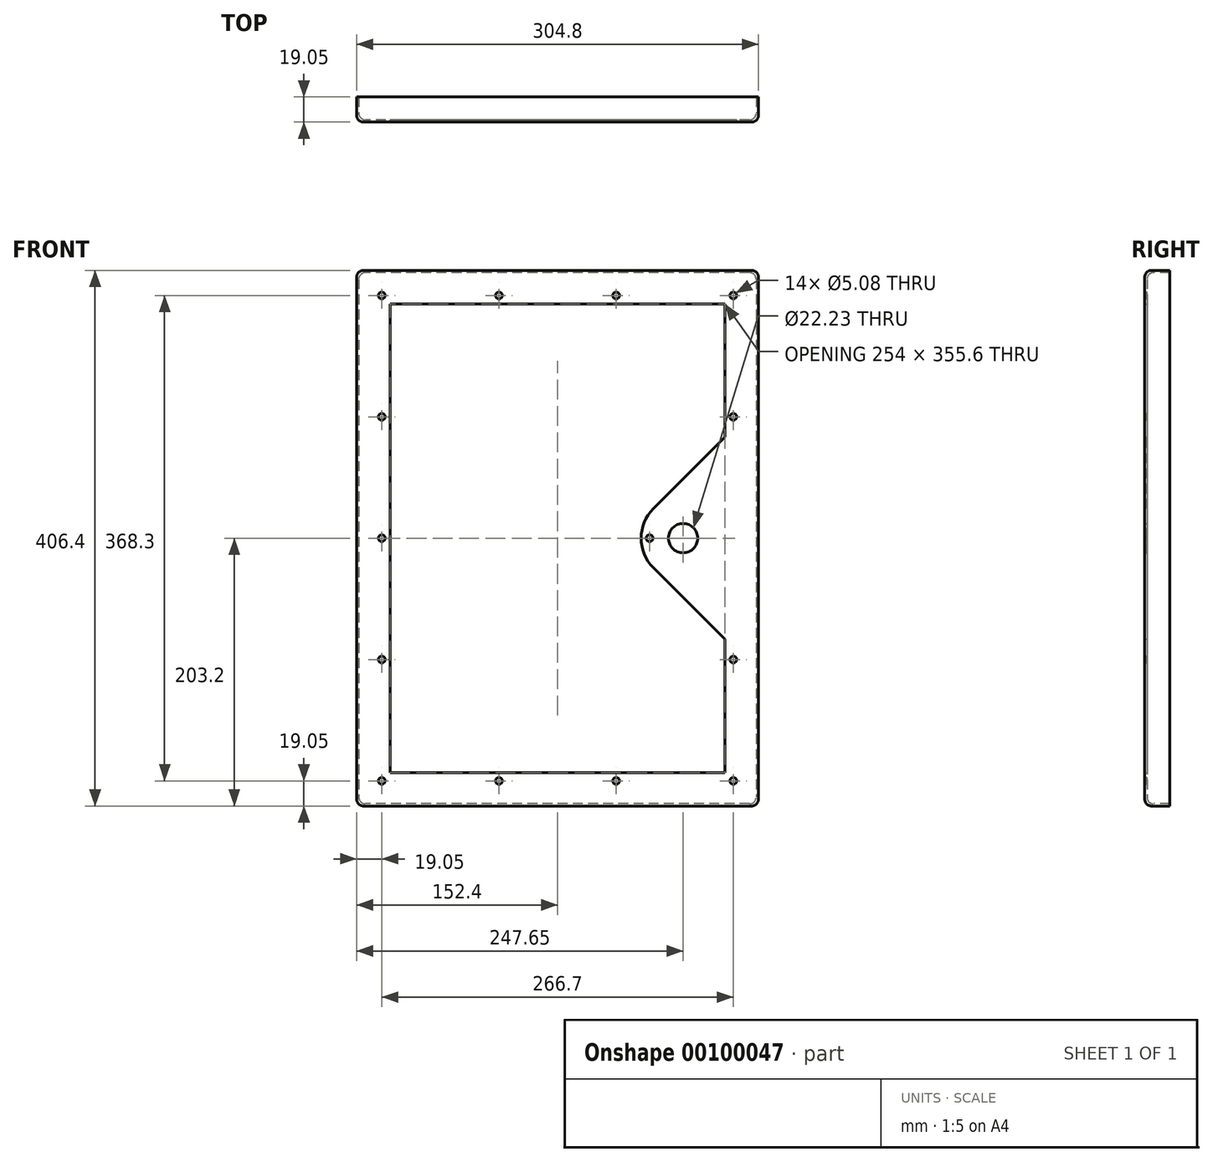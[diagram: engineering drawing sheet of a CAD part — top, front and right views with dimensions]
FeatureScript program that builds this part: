
annotation { "Feature Type Name" : "Feature", "Feature Type Description" : "" }
export const myFeature = defineFeature(function(context is Context, id is Id, definition is map)
    precondition{}
    {
        {
            var Q0;
            Q0=qCreatedBy(makeId("Front.planeOp"),FACE);
            var sketch = newSketch(context, id + "F0", { "sketchPlane" : qUnion([Q0])});
            skLineSegment(sketch, "E0.bottom", {"start": v(152.4, 203.2) * mm, "end": v(-152.4, 203.2) * mm});
            skLineSegment(sketch, "E0.top", {"start": v(152.4, -203.2) * mm, "end": v(-152.4, -203.2) * mm});
            skLineSegment(sketch, "E0.left", {"start": v(152.4, 203.2) * mm, "end": v(152.4, -203.2) * mm});
            skLineSegment(sketch, "E0.right", {"start": v(-152.4, 203.2) * mm, "end": v(-152.4, -203.2) * mm});
            skPoint(sketch, "E0.middle", {"position": v(0, 0) * mm});
            skLineSegment(sketch, "E1.bottom", {"start": v(127, 177.8) * mm, "end": v(-127, 177.8) * mm});
            skLineSegment(sketch, "E1.top", {"start": v(127, -177.8) * mm, "end": v(-127, -177.8) * mm});
            skLineSegment(sketch, "E1.left", {"start": v(127, 177.8) * mm, "end": v(127, 76.65) * mm});
            skLineSegment(sketch, "E1.right", {"start": v(-127, 177.8) * mm, "end": v(-127, -177.8) * mm});
            skArc(sketch, "E2", {"start": v(72.8, 22.45) * mm, "mid": v(63.5, 0) * mm, "end": v(72.8, -22.45) * mm});
            skLineSegment(sketch, "E3", {"start": v(72.8, 22.45) * mm, "end": v(127, 76.65) * mm});
            skLineSegment(sketch, "E4", {"start": v(72.8, -22.45) * mm, "end": v(127, -76.65) * mm});
            skLineSegment(sketch, "E5.trimOffspring", {"start": v(127, -76.65) * mm, "end": v(127, -177.8) * mm});
            skCircle(sketch, "E6", {"center": v(95.25, 0) * mm, "radius": 11.11 * mm});
            skSolve(sketch);
        }
        {
            var Q0;
            Q0=makeQuery(id+"F0.imprint","IMPRINT",FACE,{"disambiguationData":[TD([[makeQuery(id+"F0.imprint","IMPRINT",EDGE,{"derivedFrom":sQuery(id+"F0.wireOp",EDGE,"E0.bottom")}),1.0]])]});
            extrude(context, id + "F1", {"entities" : qUnion([Q0]), "depth" : 1.65 * mm});
        }
        {
            var Q0;
            Q0=makeQuery(id+"F1.opExtrude","CAP_FACE",FACE,{"disambiguationData":[OSD([sQuery(id+"F0.wireOp",EDGE,"E0.bottom"),sQuery(id+"F0.wireOp",EDGE,"E0.top"),sQuery(id+"F0.wireOp",EDGE,"E0.left"),sQuery(id+"F0.wireOp",EDGE,"E0.right"),sQuery(id+"F0.wireOp",EDGE,"E1.bottom"),sQuery(id+"F0.wireOp",EDGE,"E1.top"),sQuery(id+"F0.wireOp",EDGE,"E1.left"),sQuery(id+"F0.wireOp",EDGE,"E1.right"),sQuery(id+"F0.wireOp",EDGE,"E2"),sQuery(id+"F0.wireOp",EDGE,"E3"),sQuery(id+"F0.wireOp",EDGE,"E4"),sQuery(id+"F0.wireOp",EDGE,"E5.trimOffspring"),sQuery(id+"F0.wireOp",EDGE,"E6")])],"isStart":false});
            var sketch = newSketch(context, id + "F2", { "sketchPlane" : qUnion([Q0])});
            skLineSegment(sketch, "E7.0", {"start": v(152.4, -203.2) * mm, "end": v(-152.4, -203.2) * mm});
            skLineSegment(sketch, "E7.1", {"start": v(152.4, 203.2) * mm, "end": v(152.4, -203.2) * mm});
            skLineSegment(sketch, "E7.2", {"start": v(152.4, 203.2) * mm, "end": v(-152.4, 203.2) * mm});
            skLineSegment(sketch, "E7.3", {"start": v(-152.4, 203.2) * mm, "end": v(-152.4, -203.2) * mm});
            skLineSegment(sketch, "E8.0", {"start": v(150.75, -201.55) * mm, "end": v(-150.75, -201.55) * mm});
            skLineSegment(sketch, "E8.1", {"start": v(150.75, 201.55) * mm, "end": v(150.75, -201.55) * mm});
            skLineSegment(sketch, "E8.2", {"start": v(150.75, 201.55) * mm, "end": v(-150.75, 201.55) * mm});
            skLineSegment(sketch, "E8.3", {"start": v(-150.75, 201.55) * mm, "end": v(-150.75, -201.55) * mm});
            skSolve(sketch);
        }
        {
            var Q0;
            Q0 = qSketchRegion(id + "F2", true);
            extrude(context, id + "F3", {"entities" : qUnion([Q0]), "operationType" : NewBodyOperationType.ADD, "oppositeDirection" : true, "depth" : 19.05 * mm});
        }
        {
            var Q0;
            Q0=makeQuery(id+"F3.boolean.opBoolean","INTERSECT",EDGE,{"derivedFrom":[makeQuery(id+"F1.opExtrude","CAP_FACE",FACE,{"disambiguationData":[OSD([sQuery(id+"F0.wireOp",EDGE,"E0.bottom"),sQuery(id+"F0.wireOp",EDGE,"E0.top"),sQuery(id+"F0.wireOp",EDGE,"E0.left"),sQuery(id+"F0.wireOp",EDGE,"E0.right"),sQuery(id+"F0.wireOp",EDGE,"E1.bottom"),sQuery(id+"F0.wireOp",EDGE,"E1.top"),sQuery(id+"F0.wireOp",EDGE,"E1.left"),sQuery(id+"F0.wireOp",EDGE,"E1.right"),sQuery(id+"F0.wireOp",EDGE,"E2"),sQuery(id+"F0.wireOp",EDGE,"E3"),sQuery(id+"F0.wireOp",EDGE,"E4"),sQuery(id+"F0.wireOp",EDGE,"E5.trimOffspring"),sQuery(id+"F0.wireOp",EDGE,"E6")])],"isStart":true}),makeQuery(id+"F3.opExtrude","SWEPT_FACE",FACE,{"disambiguationData":[OSD([sQuery(id+"F2.wireOp",EDGE,"E8.3")])]})]});
            var Q1;
            Q1=makeQuery(id+"F3.boolean.opBoolean","INTERSECT",EDGE,{"derivedFrom":[makeQuery(id+"F1.opExtrude","CAP_FACE",FACE,{"disambiguationData":[OSD([sQuery(id+"F0.wireOp",EDGE,"E0.bottom"),sQuery(id+"F0.wireOp",EDGE,"E0.top"),sQuery(id+"F0.wireOp",EDGE,"E0.left"),sQuery(id+"F0.wireOp",EDGE,"E0.right"),sQuery(id+"F0.wireOp",EDGE,"E1.bottom"),sQuery(id+"F0.wireOp",EDGE,"E1.top"),sQuery(id+"F0.wireOp",EDGE,"E1.left"),sQuery(id+"F0.wireOp",EDGE,"E1.right"),sQuery(id+"F0.wireOp",EDGE,"E2"),sQuery(id+"F0.wireOp",EDGE,"E3"),sQuery(id+"F0.wireOp",EDGE,"E4"),sQuery(id+"F0.wireOp",EDGE,"E5.trimOffspring"),sQuery(id+"F0.wireOp",EDGE,"E6")])],"isStart":true}),makeQuery(id+"F3.opExtrude","SWEPT_FACE",FACE,{"disambiguationData":[OSD([sQuery(id+"F2.wireOp",EDGE,"E8.2")])]})]});
            var Q2;
            Q2=makeQuery(id+"F3.boolean.opBoolean","INTERSECT",EDGE,{"derivedFrom":[makeQuery(id+"F1.opExtrude","CAP_FACE",FACE,{"disambiguationData":[OSD([sQuery(id+"F0.wireOp",EDGE,"E0.bottom"),sQuery(id+"F0.wireOp",EDGE,"E0.top"),sQuery(id+"F0.wireOp",EDGE,"E0.left"),sQuery(id+"F0.wireOp",EDGE,"E0.right"),sQuery(id+"F0.wireOp",EDGE,"E1.bottom"),sQuery(id+"F0.wireOp",EDGE,"E1.top"),sQuery(id+"F0.wireOp",EDGE,"E1.left"),sQuery(id+"F0.wireOp",EDGE,"E1.right"),sQuery(id+"F0.wireOp",EDGE,"E2"),sQuery(id+"F0.wireOp",EDGE,"E3"),sQuery(id+"F0.wireOp",EDGE,"E4"),sQuery(id+"F0.wireOp",EDGE,"E5.trimOffspring"),sQuery(id+"F0.wireOp",EDGE,"E6")])],"isStart":true}),makeQuery(id+"F3.opExtrude","SWEPT_FACE",FACE,{"disambiguationData":[OSD([sQuery(id+"F2.wireOp",EDGE,"E8.1")])]})]});
            var Q3;
            Q3=makeQuery(id+"F3.boolean.opBoolean","INTERSECT",EDGE,{"derivedFrom":[makeQuery(id+"F1.opExtrude","CAP_FACE",FACE,{"disambiguationData":[OSD([sQuery(id+"F0.wireOp",EDGE,"E0.bottom"),sQuery(id+"F0.wireOp",EDGE,"E0.top"),sQuery(id+"F0.wireOp",EDGE,"E0.left"),sQuery(id+"F0.wireOp",EDGE,"E0.right"),sQuery(id+"F0.wireOp",EDGE,"E1.bottom"),sQuery(id+"F0.wireOp",EDGE,"E1.top"),sQuery(id+"F0.wireOp",EDGE,"E1.left"),sQuery(id+"F0.wireOp",EDGE,"E1.right"),sQuery(id+"F0.wireOp",EDGE,"E2"),sQuery(id+"F0.wireOp",EDGE,"E3"),sQuery(id+"F0.wireOp",EDGE,"E4"),sQuery(id+"F0.wireOp",EDGE,"E5.trimOffspring"),sQuery(id+"F0.wireOp",EDGE,"E6")])],"isStart":true}),makeQuery(id+"F3.opExtrude","SWEPT_FACE",FACE,{"disambiguationData":[OSD([sQuery(id+"F2.wireOp",EDGE,"E8.0")])]})]});
            var Q4;
            Q4=makeQuery(id+"F3.opExtrude","SWEPT_EDGE",EDGE,{"disambiguationData":[OSD([sQuery(id+"F2.wireOp",EDGE,"E8.0"),sQuery(id+"F2.wireOp",EDGE,"E8.3")])]});
            var Q5;
            Q5=makeQuery(id+"F3.opExtrude","SWEPT_EDGE",EDGE,{"disambiguationData":[OSD([sQuery(id+"F2.wireOp",EDGE,"E8.2"),sQuery(id+"F2.wireOp",EDGE,"E8.3")])]});
            var Q6;
            Q6=makeQuery(id+"F3.opExtrude","SWEPT_EDGE",EDGE,{"disambiguationData":[OSD([sQuery(id+"F2.wireOp",EDGE,"E8.1"),sQuery(id+"F2.wireOp",EDGE,"E8.2")])]});
            var Q7;
            Q7=makeQuery(id+"F3.opExtrude","SWEPT_EDGE",EDGE,{"disambiguationData":[OSD([sQuery(id+"F2.wireOp",EDGE,"E8.0"),sQuery(id+"F2.wireOp",EDGE,"E8.1")])]});
            fillet(context, id + "F4", {"entities" : qUnion([Q0, Q1, Q2, Q3, Q4, Q5, Q6, Q7]), "radius" : 5.08 * mm, "tangentPropagation" : true, "allowEdgeOverflow" : false});
        }
        {
            var Q0;
            Q0=makeQuery(id+"F3.boolean.opBoolean","MERGE",EDGE,{"derivedFrom":[makeQuery(id+"F1.opExtrude","SWEPT_EDGE",EDGE,{"disambiguationData":[OSD([sQuery(id+"F0.wireOp",EDGE,"E0.bottom"),sQuery(id+"F0.wireOp",EDGE,"E0.right")])]}),makeQuery(id+"F3.opExtrude","SWEPT_EDGE",EDGE,{"disambiguationData":[OSD([sQuery(id+"F2.wireOp",EDGE,"E7.2"),sQuery(id+"F2.wireOp",EDGE,"E7.3")])]})]});
            var Q1;
            Q1=makeQuery(id+"F1.opExtrude","CAP_EDGE",EDGE,{"disambiguationData":[OSD([sQuery(id+"F0.wireOp",EDGE,"E0.bottom")])],"isStart":false});
            var Q2;
            Q2=makeQuery(id+"F1.opExtrude","CAP_EDGE",EDGE,{"disambiguationData":[OSD([sQuery(id+"F0.wireOp",EDGE,"E0.right")])],"isStart":false});
            var Q3;
            Q3=makeQuery(id+"F3.boolean.opBoolean","MERGE",EDGE,{"derivedFrom":[makeQuery(id+"F1.opExtrude","SWEPT_EDGE",EDGE,{"disambiguationData":[OSD([sQuery(id+"F0.wireOp",EDGE,"E0.bottom"),sQuery(id+"F0.wireOp",EDGE,"E0.left")])]}),makeQuery(id+"F3.opExtrude","SWEPT_EDGE",EDGE,{"disambiguationData":[OSD([sQuery(id+"F2.wireOp",EDGE,"E7.1"),sQuery(id+"F2.wireOp",EDGE,"E7.2")])]})]});
            var Q4;
            Q4=makeQuery(id+"F1.opExtrude","CAP_EDGE",EDGE,{"disambiguationData":[OSD([sQuery(id+"F0.wireOp",EDGE,"E0.left")])],"isStart":false});
            var Q5;
            Q5=makeQuery(id+"F3.boolean.opBoolean","MERGE",EDGE,{"derivedFrom":[makeQuery(id+"F1.opExtrude","SWEPT_EDGE",EDGE,{"disambiguationData":[OSD([sQuery(id+"F0.wireOp",EDGE,"E0.top"),sQuery(id+"F0.wireOp",EDGE,"E0.left")])]}),makeQuery(id+"F3.opExtrude","SWEPT_EDGE",EDGE,{"disambiguationData":[OSD([sQuery(id+"F2.wireOp",EDGE,"E7.0"),sQuery(id+"F2.wireOp",EDGE,"E7.1")])]})]});
            var Q6;
            Q6=makeQuery(id+"F1.opExtrude","CAP_EDGE",EDGE,{"disambiguationData":[OSD([sQuery(id+"F0.wireOp",EDGE,"E0.top")])],"isStart":false});
            var Q7;
            Q7=makeQuery(id+"F3.boolean.opBoolean","MERGE",EDGE,{"derivedFrom":[makeQuery(id+"F1.opExtrude","SWEPT_EDGE",EDGE,{"disambiguationData":[OSD([sQuery(id+"F0.wireOp",EDGE,"E0.top"),sQuery(id+"F0.wireOp",EDGE,"E0.right")])]}),makeQuery(id+"F3.opExtrude","SWEPT_EDGE",EDGE,{"disambiguationData":[OSD([sQuery(id+"F2.wireOp",EDGE,"E7.0"),sQuery(id+"F2.wireOp",EDGE,"E7.3")])]})]});
            fillet(context, id + "F5", {"entities" : qUnion([Q0, Q1, Q2, Q3, Q4, Q5, Q6, Q7]), "radius" : 5.08 * mm, "tangentPropagation" : true, "allowEdgeOverflow" : false});
        }
        {
            var Q0;
            Q0=makeQuery(id+"F1.opExtrude","CAP_FACE",FACE,{"disambiguationData":[OSD([sQuery(id+"F0.wireOp",EDGE,"E0.bottom"),sQuery(id+"F0.wireOp",EDGE,"E0.top"),sQuery(id+"F0.wireOp",EDGE,"E0.left"),sQuery(id+"F0.wireOp",EDGE,"E0.right"),sQuery(id+"F0.wireOp",EDGE,"E1.bottom"),sQuery(id+"F0.wireOp",EDGE,"E1.top"),sQuery(id+"F0.wireOp",EDGE,"E1.left"),sQuery(id+"F0.wireOp",EDGE,"E1.right"),sQuery(id+"F0.wireOp",EDGE,"E2"),sQuery(id+"F0.wireOp",EDGE,"E3"),sQuery(id+"F0.wireOp",EDGE,"E4"),sQuery(id+"F0.wireOp",EDGE,"E5.trimOffspring"),sQuery(id+"F0.wireOp",EDGE,"E6")])],"isStart":false});
            var sketch = newSketch(context, id + "F6", { "sketchPlane" : qUnion([Q0])});
            skCircle(sketch, "E9", {"center": v(-133.35, 184.15) * mm, "radius": 2.54 * mm});
            skCircle(sketch, "E10", {"center": v(-133.35, 92.08) * mm, "radius": 2.54 * mm});
            skCircle(sketch, "E11", {"center": v(-133.35, 0) * mm, "radius": 2.54 * mm});
            skCircle(sketch, "E12", {"center": v(-133.35, -92.08) * mm, "radius": 2.54 * mm});
            skCircle(sketch, "E13", {"center": v(-133.35, -184.15) * mm, "radius": 2.54 * mm});
            skCircle(sketch, "E14", {"center": v(-44.45, 184.15) * mm, "radius": 2.54 * mm});
            skCircle(sketch, "E15", {"center": v(44.45, 184.15) * mm, "radius": 2.54 * mm});
            skCircle(sketch, "E16", {"center": v(133.35, 184.15) * mm, "radius": 2.54 * mm});
            skCircle(sketch, "E17", {"center": v(133.35, 92.08) * mm, "radius": 2.54 * mm});
            skCircle(sketch, "E18", {"center": v(133.35, -92.07) * mm, "radius": 2.54 * mm});
            skCircle(sketch, "E19", {"center": v(133.35, -184.15) * mm, "radius": 2.54 * mm});
            skCircle(sketch, "E20", {"center": v(44.45, -184.15) * mm, "radius": 2.54 * mm});
            skCircle(sketch, "E21", {"center": v(-44.45, -184.15) * mm, "radius": 2.54 * mm});
            skCircle(sketch, "E22", {"center": v(69.85, 0) * mm, "radius": 2.54 * mm});
            skLineSegment(sketch, "E23", {"start": v(-133.35, 184.15) * mm, "end": v(-44.45, 184.15) * mm, "construction": true});
            skLineSegment(sketch, "E24", {"start": v(-44.45, 184.15) * mm, "end": v(44.45, 184.15) * mm, "construction": true});
            skLineSegment(sketch, "E25", {"start": v(44.45, 184.15) * mm, "end": v(133.35, 184.15) * mm, "construction": true});
            skLineSegment(sketch, "E26", {"start": v(-133.35, 184.15) * mm, "end": v(-133.35, 92.08) * mm, "construction": true});
            skLineSegment(sketch, "E27", {"start": v(-133.35, 92.08) * mm, "end": v(-133.35, 0) * mm, "construction": true});
            skLineSegment(sketch, "E28", {"start": v(-133.35, 0) * mm, "end": v(-133.35, -92.08) * mm, "construction": true});
            skLineSegment(sketch, "E29", {"start": v(-133.35, -92.08) * mm, "end": v(-133.35, -184.15) * mm, "construction": true});
            skSolve(sketch);
        }
        {
            var Q0;
            Q0 = qSketchRegion(id + "F6", true);
            extrude(context, id + "F7", {"entities" : qUnion([Q0]), "operationType" : NewBodyOperationType.REMOVE, "oppositeDirection" : true, "depth" : 25.4 * mm});
        }
    });
